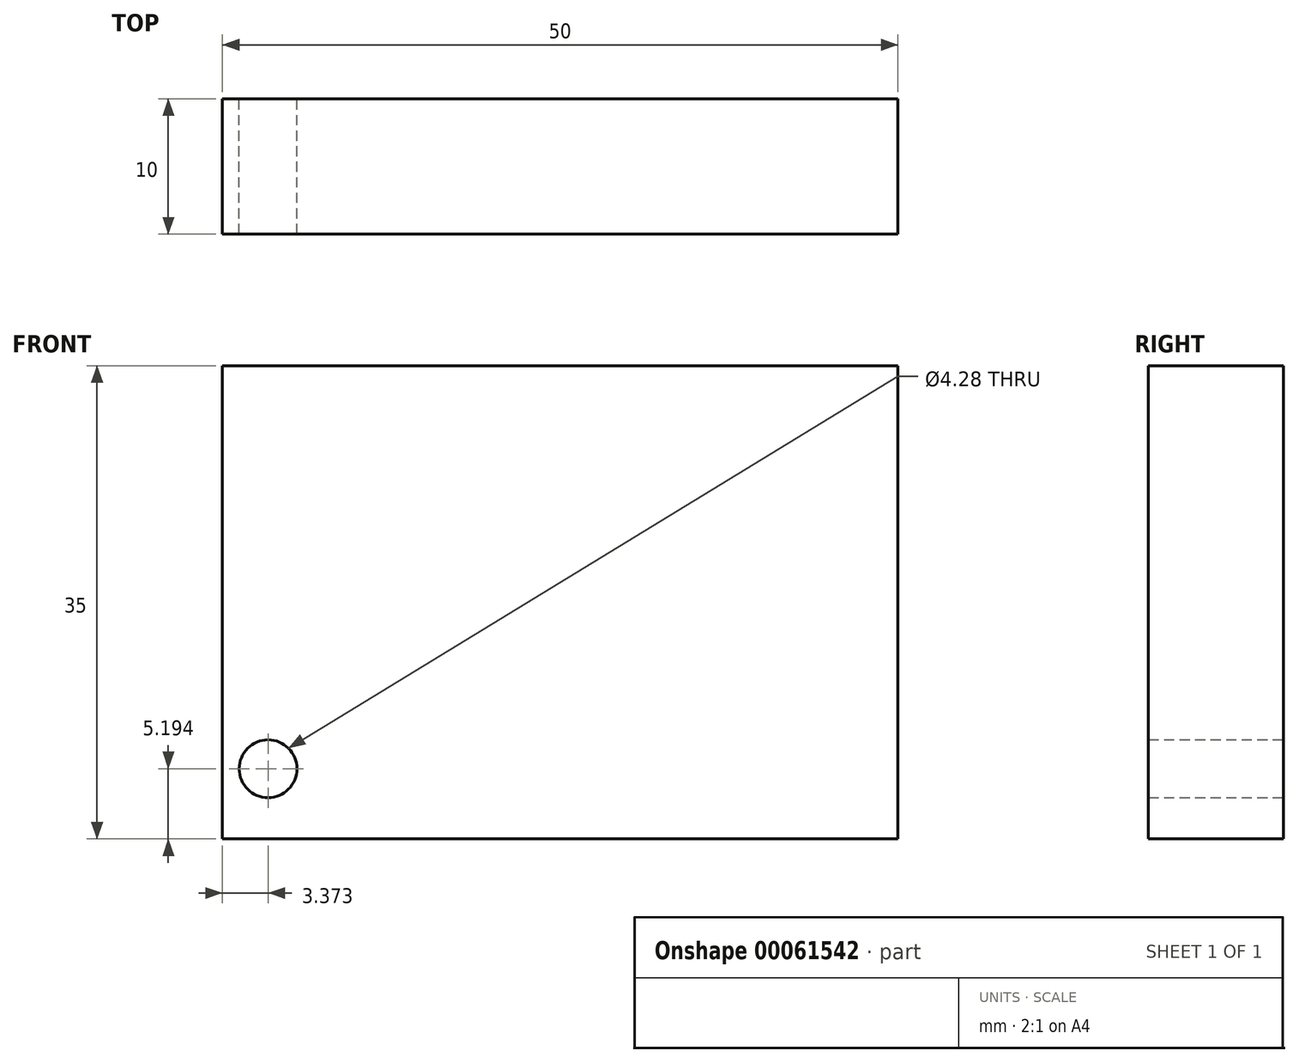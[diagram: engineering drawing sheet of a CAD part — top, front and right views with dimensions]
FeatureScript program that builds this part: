
annotation { "Feature Type Name" : "Feature", "Feature Type Description" : "" }
export const myFeature = defineFeature(function(context is Context, id is Id, definition is map)
    precondition{}
    {
        {
            var Q0;
            Q0=qCreatedBy(makeId("Front.planeOp"),FACE);
            var sketch = newSketch(context, id + "F0", { "sketchPlane" : qUnion([Q0])});
            skLineSegment(sketch, "E0.bottom", {"start": v(-49.48, 38.83) * mm, "end": v(0.52, 38.83) * mm});
            skLineSegment(sketch, "E0.top", {"start": v(-49.48, 3.83) * mm, "end": v(0.52, 3.83) * mm});
            skLineSegment(sketch, "E0.left", {"start": v(-49.48, 38.83) * mm, "end": v(-49.48, 3.83) * mm});
            skLineSegment(sketch, "E0.right", {"start": v(0.52, 38.83) * mm, "end": v(0.52, 3.83) * mm});
            skCircle(sketch, "E1", {"center": v(-46.1, 9.02) * mm, "radius": 2.14 * mm});
            skSolve(sketch);
        }
        {
            var Q0;
            Q0=makeQuery(id+"F0.imprint","IMPRINT",FACE,{"disambiguationData":[TD([[makeQuery(id+"F0.imprint","IMPRINT",EDGE,{"derivedFrom":sQuery(id+"F0.wireOp",EDGE,"E0.bottom")}),-1.0]])]});
            extrude(context, id + "F1", {"entities" : qUnion([Q0]), "depth" : 10 * mm});
        }
    });
